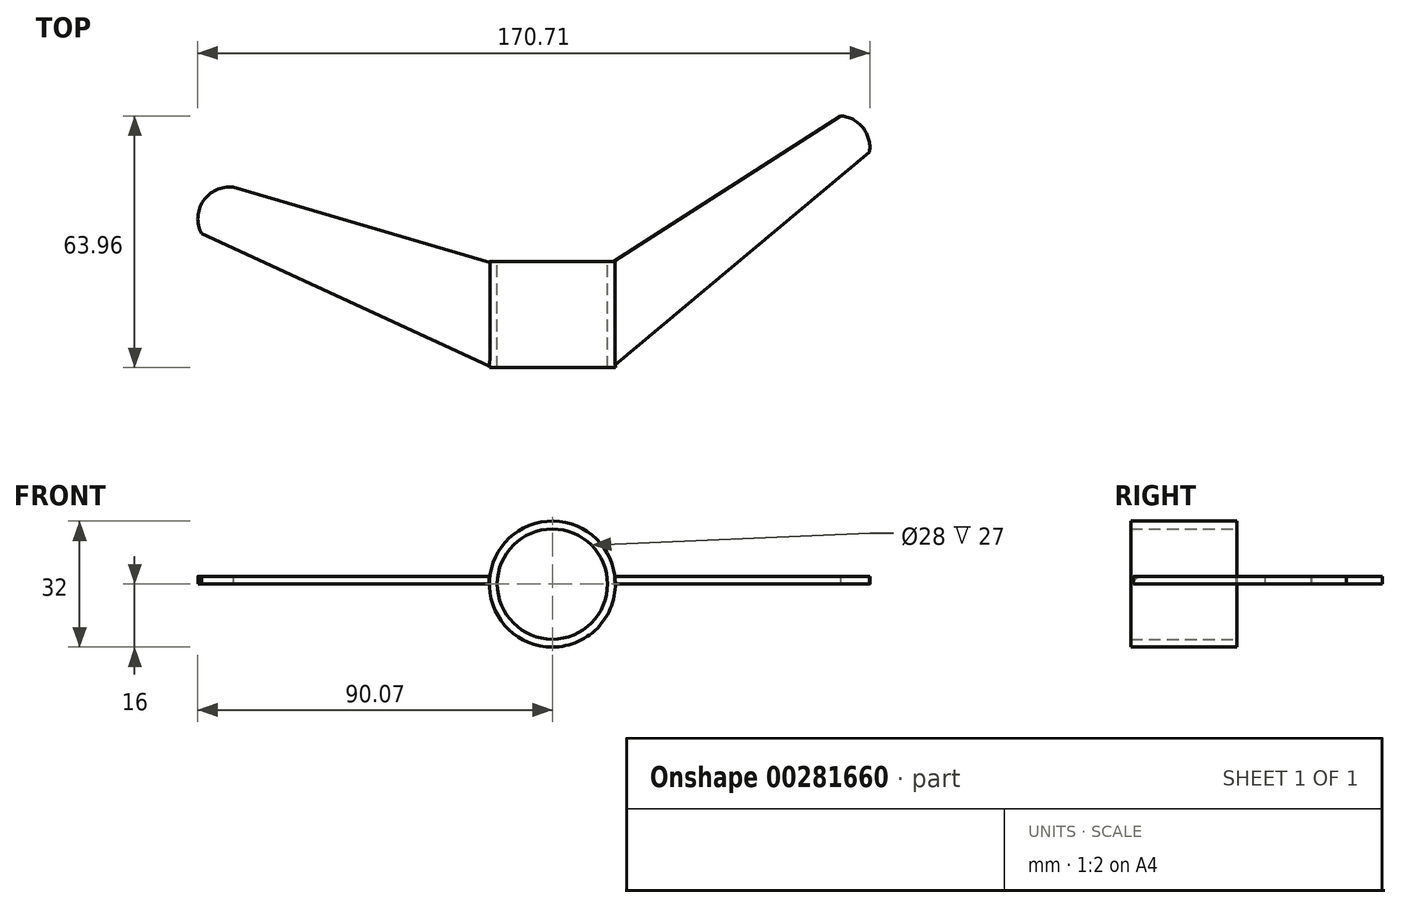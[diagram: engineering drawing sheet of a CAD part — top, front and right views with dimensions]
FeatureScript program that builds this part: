
annotation { "Feature Type Name" : "Feature", "Feature Type Description" : "" }
export const myFeature = defineFeature(function(context is Context, id is Id, definition is map)
    precondition{}
    {
        {
            var Q0;
            Q0=qCreatedBy(makeId("Front.planeOp"),FACE);
            var sketch = newSketch(context, id + "F0", { "sketchPlane" : qUnion([Q0])});
            skCircle(sketch, "E0", {"center": v(0, 0) * mm, "radius": 14 * mm});
            skSolve(sketch);
        }
        {
            var Q0;
            Q0 = qSketchRegion(id + "F0", true);
            extrude(context, id + "F1", {"entities" : qUnion([Q0]), "depth" : 25 * mm});
        }
        {
            var Q0;
            Q0=makeQuery(id+"F1.opExtrude","CAP_FACE",FACE,{"disambiguationData":[OSD([sQuery(id+"F0.wireOp",EDGE,"E0")])],"isStart":false});
            shell(context, id + "F2", {"entities" : qUnion([Q0]), "thickness" : 2 * mm, "oppositeDirection" : true});
        }
        {
            var Q0;
            {var subQ0=sQuery(id+"F0.wireOp",EDGE,"E0");Q0=makeQuery(id+"F2.opShell","OFFSET_FACE",FACE,{"disambiguationData":[OSD([subQ0]),TDD([makeQuery(id+"F1.opExtrude","CAP_FACE",FACE,{"disambiguationData":[OSD([subQ0])],"isStart":true})])]});}
            extrude(context, id + "F3", {"entities" : qUnion([Q0]), "operationType" : NewBodyOperationType.REMOVE, "endBound" : BoundingType.THROUGH_ALL, "oppositeDirection" : true, "depth" : 25 * mm});
        }
        {
            var Q0;
            Q0=qCreatedBy(makeId("Top.planeOp"),FACE);
            var sketch = newSketch(context, id + "F4", { "sketchPlane" : qUnion([Q0])});
            skLineSegment(sketch, "E1", {"start": v(-14, 1.1) * mm, "end": v(-81.17, 20.81) * mm});
            skArc(sketch, "E2", {"start": v(-81.17, 20.81) * mm, "mid": v(-88.68, 17.36) * mm, "end": v(-89.12, 9.1) * mm});
            skLineSegment(sketch, "E3", {"start": v(-89.12, 9.1) * mm, "end": v(-16.02, -24.65) * mm});
            skLineSegment(sketch, "E4", {"start": v(14.22, 1.17) * mm, "end": v(73.14, 38.96) * mm});
            skArc(sketch, "E5", {"start": v(73.14, 38.96) * mm, "mid": v(78.86, 36.01) * mm, "end": v(80.56, 29.8) * mm});
            skLineSegment(sketch, "E6", {"start": v(80.56, 29.8) * mm, "end": v(15.5, -24.66) * mm});
            skLineSegment(sketch, "E7", {"start": v(-14, 1.1) * mm, "end": v(-16.02, -24.65) * mm});
            skLineSegment(sketch, "E8", {"start": v(14.22, 1.17) * mm, "end": v(15.5, -24.66) * mm});
            skSolve(sketch);
        }
        {
            var Q0;
            Q0 = qSketchRegion(id + "F4", true);
            extrude(context, id + "F5", {"entities" : qUnion([Q0]), "operationType" : NewBodyOperationType.ADD, "depth" : 2 * mm});
        }
    });
